# Revit family: AB-QM_DN40-50_External_AMV(E) 25 SD(SU)_RFA_1
name_source: partatom
category: Pipe Accessories
units: mm (PartAtom-declared; Revit-internal decimal feet)

## family parameters
Always vertical = Yes
Cut with Voids When Loaded = No
OmniClass Number = 23.65.55.14.17
OmniClass Title = Adjusting/Controlling Valves for Liquid Services
Part Type = Valve - Breaks Into
Round Connector Dimension = Use Diameter
Shared = No
Work Plane-Based = No

## types (2) — shared parameters
082H3037 = AMV(E) 25 SD(SU)_RFA : AMV 25 SD_230V_082H3037
082H3038 = AMV(E) 25 SD(SU)_RFA : AME 25 SD_082H3038
082H3040 = AMV(E) 25 SD(SU)_RFA : AMV 25 SU_230V_082H3040
082H3041 = AMV(E) 25 SD(SU)_RFA : AME 25 SU_082H3041
Adapter Type = Adapter_AMV(E) 15(25)(35)_RFA : Adapter_AMV(E) 25_DN40-100_003Z0694
CenSd_RB2_6 = 23 mm  [stored 0.0754593 ft]
CenSd_RB5_6 = 26 mm  [stored 0.0853018 ft]
CenSd_RN1_6 = 13 mm  [stored 0.0426509 ft]
Connection = External Thread (ISO 228/1)
D1 = 65 mm
Description = Pressure Independent Control Valve
H1 = 156 mm
H1N = 3 mm  [stored 0.00984252 ft]
H1N2 = 7 mm  [stored 0.0229659 ft]
H1N2__ve = -7 mm  [stored -0.0229659 ft]
H1N3 = 14 mm  [stored 0.0459318 ft]
H1N3__ve = -14 mm
H1N__ve = -3 mm  [stored -0.00984252 ft]
H1_1 = 3 mm  [stored 0.00984252 ft]
H1_2 = 2 mm  [stored 0.00656168 ft]
H1_3 = 13 mm  [stored 0.0426509 ft]
H1_3__ve = -13 mm
H1_4 = 5 mm  [stored 0.0164042 ft]
H1_4__ve = -5 mm  [stored -0.0164042 ft]
H1_5 = 25 mm  [stored 0.082021 ft]
H1_5__ve = -25 mm  [stored -0.082021 ft]
H2 = 192 mm
H2N = 19 mm  [stored 0.062336 ft]
H2_1 = 37 mm  [stored 0.121391 ft]
H2_2 = 5 mm  [stored 0.0164042 ft]
H2_3 = 13 mm  [stored 0.0426509 ft]
H2_4 = 7 mm  [stored 0.0229659 ft]
H2_5 = 13 mm  [stored 0.0426509 ft]
H2_6 = 49 mm  [stored 0.160761 ft]
H3 = 348 mm
HB = 19 mm  [stored 0.062336 ft]
HH = 20 mm  [stored 0.0656168 ft]
HO1 = 55 mm
HO1__ve = -55 mm  [stored -0.180446 ft]
HT = 14 mm  [stored 0.0459318 ft]
HT__ve = -14 mm
IfcExportAs = IfcValveType
IfcExportType = AB-QM
L2D = 130 mm
L2D_Min = 30 mm  [stored 0.0984252 ft]
LM = 94 mm
LM_4 = 23 mm  [stored 0.0754593 ft]
LOD 200 = No
LOD 350 = Yes
MIN = 2 mm  [stored 0.00656168 ft]
MIN__ve = -2 mm  [stored -0.00656168 ft]
Manufacturer = Danfoss
Max Differential Pressure = 600 kPa
Max Medium Temperature = 120 °C
Min Differential Pressure = 30 kPa
Min Medium Temperature = 2 °C
Nominal Pressure = PN 16
R = 20 mm  [stored 0.0656168 ft]
RB = 27 mm  [stored 0.0885827 ft]
RB10 = 39 mm  [stored 0.127953 ft]
RB2 = 14 mm  [stored 0.0459318 ft]
RB2_1 = 24 mm  [stored 0.0787402 ft]
RB2_6 = 27 mm  [stored 0.0885827 ft]
RB3 = 13 mm  [stored 0.0426509 ft]
RB3_1 = 20 mm  [stored 0.0656168 ft]
RB4 = 35 mm
RB5 = 30 mm  [stored 0.0984252 ft]
RB5_1 = 37 mm  [stored 0.121391 ft]
RB6 = 57 mm
RB7 = 44 mm  [stored 0.144357 ft]
RB8 = 68 mm
RB9 = 36 mm
RH = 8 mm  [stored 0.0262467 ft]
RN1 = 13 mm  [stored 0.0426509 ft]
RN1_1 = 15 mm  [stored 0.0492126 ft]
RT1 = 3 mm  [stored 0.00984252 ft]
RT2 = 4 mm  [stored 0.0131234 ft]
RT3 = 17 mm
RTN = 7 mm  [stored 0.0229659 ft]
Setting Range = 40-100%
Stroke = 10 mm
TP_D = 14 mm  [stored 0.0459318 ft]
TP_R1 = 14 mm  [stored 0.0459318 ft]
TP_W = 78 mm
URL = https://store.danfoss.com
Valve Body Material = Danfoss Grey Iron
Voltage = 24 V
W = 146 mm
W2D = 40 mm  [stored 0.131234 ft]
XT = 2 mm  [stored 0.00656168 ft]
Z1 = 1 mm  [stored 0.00328084 ft]
Z2 = 4 mm  [stored 0.0131234 ft]

## per-type parameters (varying)
| type | Actuator Type | D | L | L1 | L1__ve | Model | Model Type | Nominal Flow | Nominal Flow (Text) | Power | R1 | R2 | RM | TP_L | Weight |
| AB-QM_DN40_External_003Z0770 | AMV(E) 25 SD(SU)_RFA : AME 25 SD_082H3038 | 40 mm  [stored 0.131234 ft] | 110 mm | 18 mm  [stored 0.0590551 ft] | -18 mm  [stored -0.0590551 ft] | 003Z0770 | AB-QM_DN40 | 7.5 m³/h | 7500 l/h | 14 VA | 30 mm  [stored 0.0984252 ft] | 48 mm  [stored 0.15748 ft] | 39 mm  [stored 0.127953 ft] | 40 mm  [stored 0.131234 ft] | 6.83 kg |
| AB-QM_DN50_External_003Z0771 | AMV(E) 25 SD(SU)_RFA : AMV 25 SD_24V_082H3036 | 50 mm | 130 mm | 22 mm  [stored 0.0721785 ft] | -22 mm  [stored -0.0721785 ft] | 003Z0771 | AB-QM_DN50 | 12.5 m³/h | 12500 l/h | 12 VA | 38 mm  [stored 0.124672 ft] | 56 mm | 48 mm  [stored 0.15748 ft] | 52 mm | 7.87 kg |

note: [stored X ft] marks values corroborated as IEEE doubles in the binary element streams (Revit-internal decimal feet)

## geometry (parser evidence)
native form markers: Sweep x4
no freeform markers — native parametric forms only
